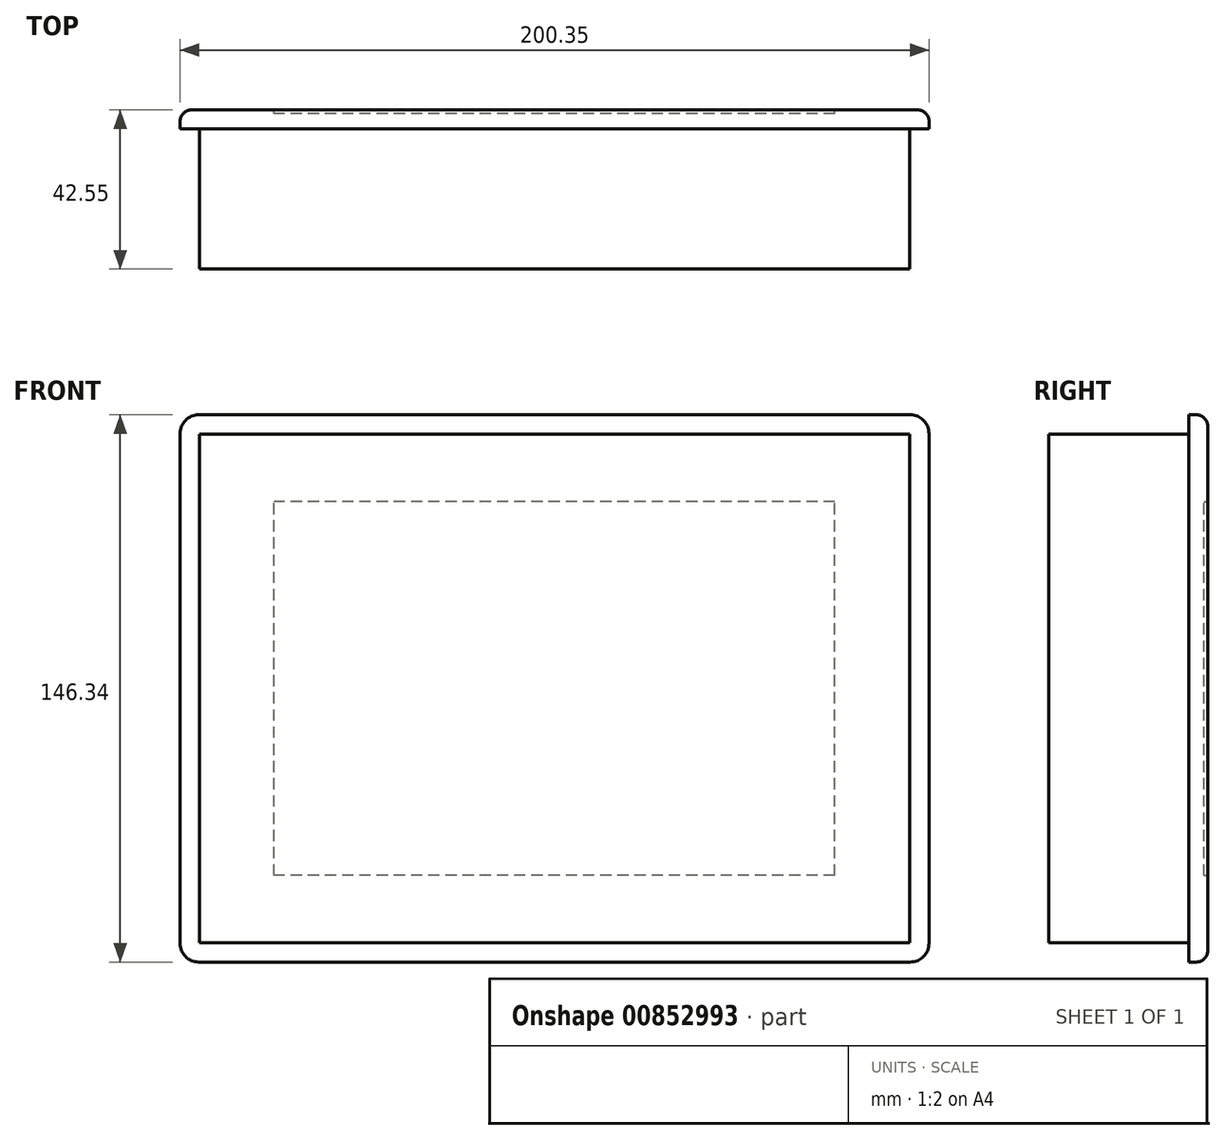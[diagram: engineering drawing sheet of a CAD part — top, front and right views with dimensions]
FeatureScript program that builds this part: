
annotation { "Feature Type Name" : "Feature", "Feature Type Description" : "" }
export const myFeature = defineFeature(function(context is Context, id is Id, definition is map)
    precondition{}
    {
        {
            var Q0;
            Q0=qCreatedBy(makeId("Front.planeOp"),FACE);
            var sketch = newSketch(context, id + "F0", { "sketchPlane" : qUnion([Q0])});
            skLineSegment(sketch, "E0.bottom", {"start": v(100.17, 73.18) * mm, "end": v(-100.17, 73.18) * mm});
            skLineSegment(sketch, "E0.top", {"start": v(100.18, -73.18) * mm, "end": v(-100.17, -73.18) * mm});
            skLineSegment(sketch, "E0.left", {"start": v(100.17, 73.18) * mm, "end": v(100.18, -73.18) * mm});
            skLineSegment(sketch, "E0.right", {"start": v(-100.17, 73.18) * mm, "end": v(-100.17, -73.18) * mm});
            skPoint(sketch, "E0.middle", {"position": v(0, 0) * mm});
            skSolve(sketch);
        }
        {
            var Q0;
            Q0=makeQuery(id+"F0.imprint","IMPRINT",FACE,{"disambiguationData":[TD([[makeQuery(id+"F0.imprint","IMPRINT",EDGE,{"derivedFrom":sQuery(id+"F0.wireOp",EDGE,"E0.bottom")}),1.0]])]});
            extrude(context, id + "F1", {"entities" : qUnion([Q0]), "depth" : 5 * mm, "offsetDistance" : 25 * mm});
        }
        {
            var Q0;
            Q0=makeQuery(id+"F1.opExtrude","SWEPT_EDGE",EDGE,{"disambiguationData":[OSD([sQuery(id+"F0.wireOp",EDGE,"E0.bottom"),sQuery(id+"F0.wireOp",EDGE,"E0.left")])]});
            var Q1;
            Q1=makeQuery(id+"F1.opExtrude","SWEPT_EDGE",EDGE,{"disambiguationData":[OSD([sQuery(id+"F0.wireOp",EDGE,"E0.bottom"),sQuery(id+"F0.wireOp",EDGE,"E0.right")])]});
            var Q2;
            Q2=makeQuery(id+"F1.opExtrude","SWEPT_EDGE",EDGE,{"disambiguationData":[OSD([sQuery(id+"F0.wireOp",EDGE,"E0.top"),sQuery(id+"F0.wireOp",EDGE,"E0.right")])]});
            var Q3;
            Q3=makeQuery(id+"F1.opExtrude","SWEPT_EDGE",EDGE,{"disambiguationData":[OSD([sQuery(id+"F0.wireOp",EDGE,"E0.top"),sQuery(id+"F0.wireOp",EDGE,"E0.left")])]});
            fillet(context, id + "F2", {"entities" : qUnion([Q0, Q1, Q2, Q3]), "radius" : 5 * mm, "tangentPropagation" : true, "allowEdgeOverflow" : false});
        }
        {
            var Q0;
            Q0=makeQuery(id+"F1.opExtrude","CAP_FACE",FACE,{"disambiguationData":[OSD([sQuery(id+"F0.wireOp",EDGE,"E0.bottom"),sQuery(id+"F0.wireOp",EDGE,"E0.top"),sQuery(id+"F0.wireOp",EDGE,"E0.left"),sQuery(id+"F0.wireOp",EDGE,"E0.right")])],"isStart":true});
            var sketch = newSketch(context, id + "F3", { "sketchPlane" : qUnion([Q0])});
            skLineSegment(sketch, "E1.bottom", {"start": v(-94.95, -67.95) * mm, "end": v(94.95, -67.95) * mm});
            skLineSegment(sketch, "E1.top", {"start": v(-94.95, 67.95) * mm, "end": v(94.95, 67.95) * mm});
            skLineSegment(sketch, "E1.left", {"start": v(-94.95, -67.95) * mm, "end": v(-94.95, 67.95) * mm});
            skLineSegment(sketch, "E1.right", {"start": v(94.95, -67.95) * mm, "end": v(94.95, 67.95) * mm});
            skPoint(sketch, "E1.middle", {"position": v(0, 0) * mm});
            skSolve(sketch);
        }
        {
            var Q0;
            Q0 = qSketchRegion(id + "F3", true);
            extrude(context, id + "F4", {"entities" : qUnion([Q0]), "operationType" : NewBodyOperationType.ADD, "oppositeDirection" : true, "depth" : 42.55 * mm, "offsetDistance" : 25 * mm});
        }
        {
            var Q0;
            Q0=makeQuery(id+"F1.opExtrude","CAP_FACE",FACE,{"disambiguationData":[OSD([sQuery(id+"F0.wireOp",EDGE,"E0.bottom"),sQuery(id+"F0.wireOp",EDGE,"E0.top"),sQuery(id+"F0.wireOp",EDGE,"E0.left"),sQuery(id+"F0.wireOp",EDGE,"E0.right")])],"isStart":true});
            fillet(context, id + "F5", {"entities" : qUnion([Q0]), "radius" : 3 * mm, "tangentPropagation" : true, "allowEdgeOverflow" : false});
        }
        {
            var Q0;
            Q0=makeQuery(id+"F1.opExtrude","CAP_FACE",FACE,{"disambiguationData":[OSD([sQuery(id+"F0.wireOp",EDGE,"E0.bottom"),sQuery(id+"F0.wireOp",EDGE,"E0.top"),sQuery(id+"F0.wireOp",EDGE,"E0.left"),sQuery(id+"F0.wireOp",EDGE,"E0.right")])],"isStart":true});
            var sketch = newSketch(context, id + "F6", { "sketchPlane" : qUnion([Q0])});
            skLineSegment(sketch, "E2.bottom", {"start": v(-75, -50) * mm, "end": v(75, -50) * mm});
            skLineSegment(sketch, "E2.top", {"start": v(-75, 50) * mm, "end": v(75, 50) * mm});
            skLineSegment(sketch, "E2.left", {"start": v(-75, -50) * mm, "end": v(-75, 50) * mm});
            skLineSegment(sketch, "E2.right", {"start": v(75, -50) * mm, "end": v(75, 50) * mm});
            skPoint(sketch, "E2.middle", {"position": v(0, 0) * mm});
            skSolve(sketch);
        }
        {
            var Q0;
            Q0=makeQuery(id+"F6.imprint","IMPRINT",FACE,{"disambiguationData":[TD([[makeQuery(id+"F6.imprint","IMPRINT",EDGE,{"derivedFrom":sQuery(id+"F6.wireOp",EDGE,"E2.bottom")}),1.0]])]});
            extrude(context, id + "F7", {"entities" : qUnion([Q0]), "operationType" : NewBodyOperationType.REMOVE, "oppositeDirection" : true, "depth" : 1 * mm, "offsetDistance" : 25 * mm});
        }
    });
